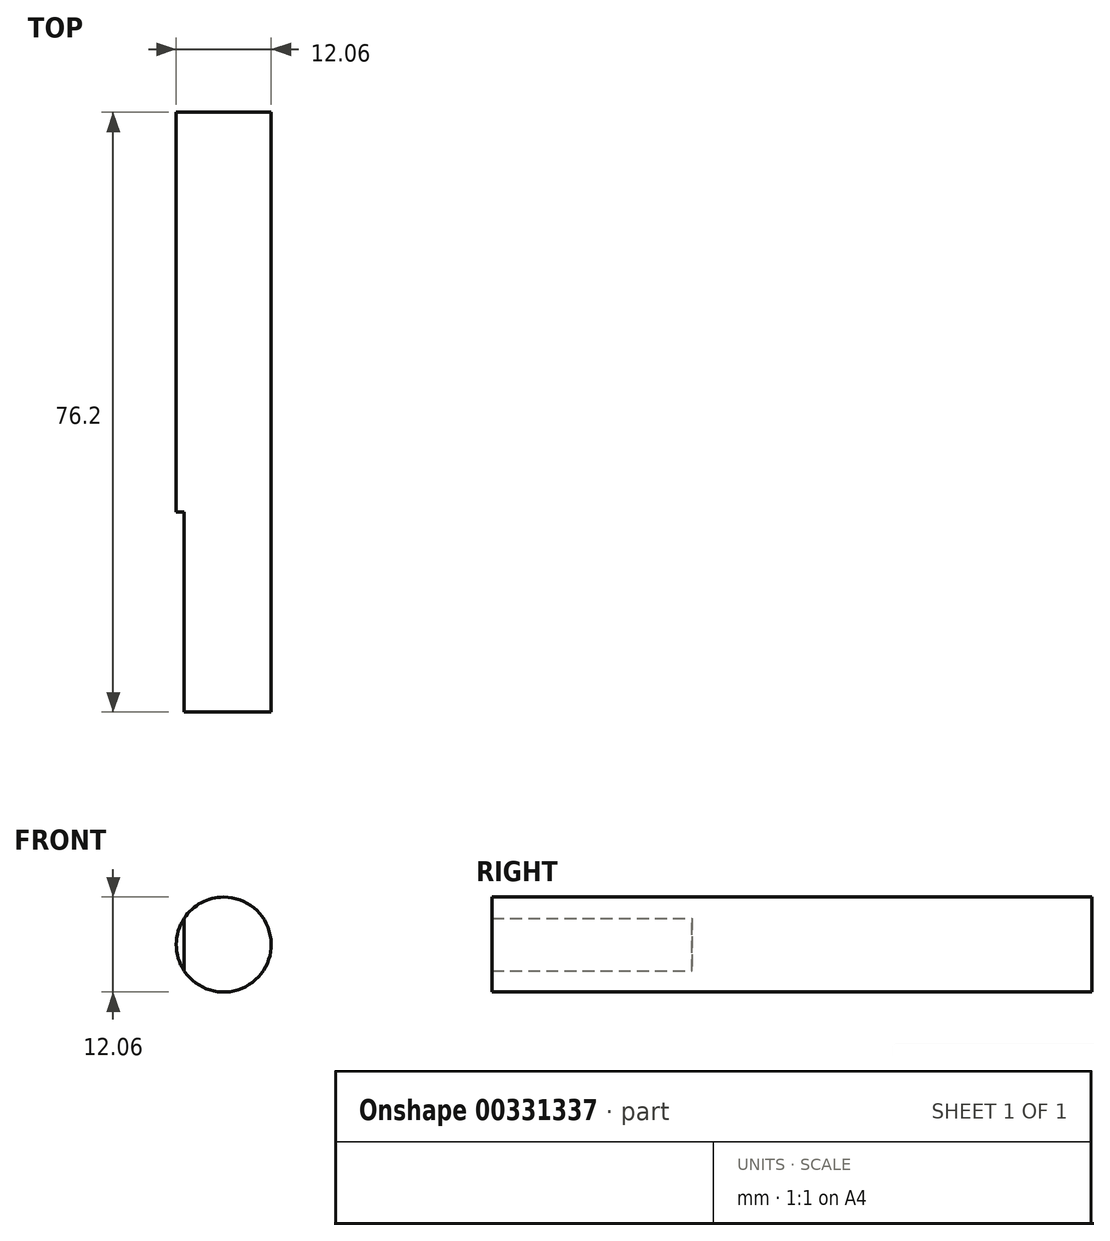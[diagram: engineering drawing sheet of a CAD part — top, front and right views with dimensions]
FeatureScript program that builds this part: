
annotation { "Feature Type Name" : "Feature", "Feature Type Description" : "" }
export const myFeature = defineFeature(function(context is Context, id is Id, definition is map)
    precondition{}
    {
        {
            var Q0;
            Q0=qCreatedBy(makeId("Front.planeOp"),FACE);
            var sketch = newSketch(context, id + "F0", { "sketchPlane" : qUnion([Q0])});
            skArc(sketch, "E0", {"start": v(-5.02, -3.35) * mm, "mid": v(6.03, 0) * mm, "end": v(-5.02, 3.35) * mm});
            skLineSegment(sketch, "E1", {"start": v(6.03, 0) * mm, "end": v(-5.02, 0) * mm, "construction": true});
            skLineSegment(sketch, "E2", {"start": v(-5.02, 3.35) * mm, "end": v(-5.02, -3.35) * mm});
            skSolve(sketch);
        }
        {
            var Q0;
            Q0=qSketchRegion(id+"F0",true);
            extrude(context, id + "F1", {"entities" : qUnion([Q0]), "depth" : 25.4 * mm});
        }
        {
            var Q0;
            Q0=makeQuery(id+"F1.opExtrude","CAP_FACE",FACE,{"disambiguationData":[OSD([sQuery(id+"F0.wireOp",EDGE,"E0"),sQuery(id+"F0.wireOp",EDGE,"E2")])],"isStart":true});
            var sketch = newSketch(context, id + "F2", { "sketchPlane" : qUnion([Q0])});
            skCircle(sketch, "E3", {"center": v(0, 0) * mm, "radius": 6.03 * mm});
            skSolve(sketch);
        }
        {
            var Q0;
            Q0=qSketchRegion(id+"F2",true);
            extrude(context, id + "F3", {"entities" : qUnion([Q0]), "operationType" : NewBodyOperationType.ADD, "depth" : 50.8 * mm});
        }
    });
